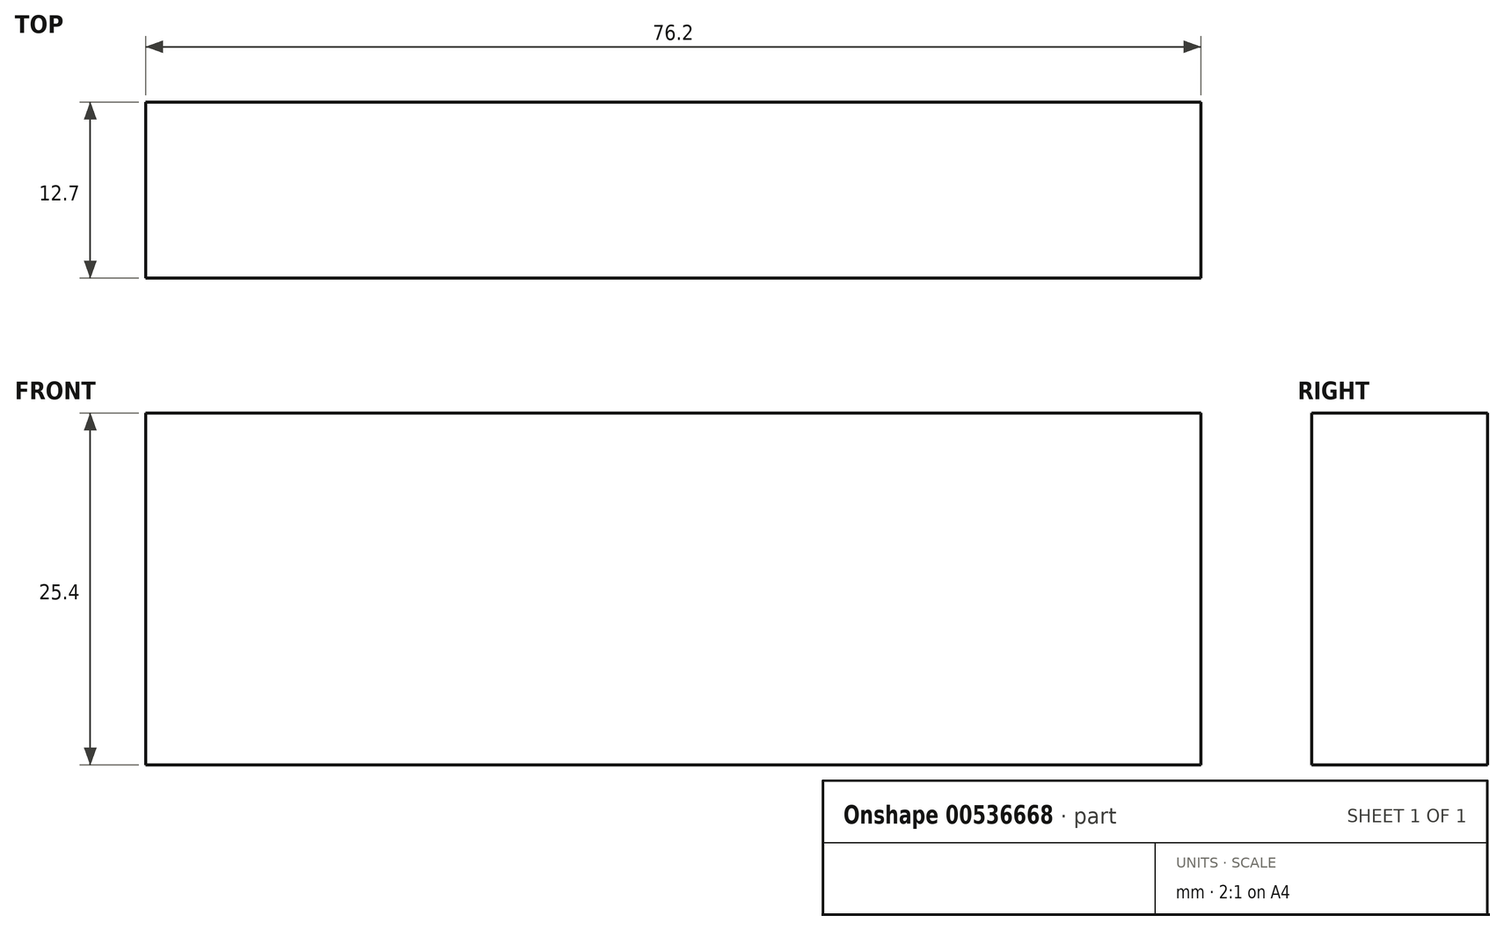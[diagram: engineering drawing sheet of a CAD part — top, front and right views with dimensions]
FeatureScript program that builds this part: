
annotation { "Feature Type Name" : "Feature", "Feature Type Description" : "" }
export const myFeature = defineFeature(function(context is Context, id is Id, definition is map)
    precondition{}
    {
        {
            var Q0;
            Q0=qCreatedBy(makeId("Front.planeOp"),FACE);
            var sketch = newSketch(context, id + "F0", { "sketchPlane" : qUnion([Q0])});
            skLineSegment(sketch, "E0", {"start": v(0, 37.65) * mm, "end": v(0, 12.25) * mm});
            skLineSegment(sketch, "E1", {"start": v(0, 37.65) * mm, "end": v(76.2, 37.65) * mm});
            skLineSegment(sketch, "E2", {"start": v(76.2, 37.65) * mm, "end": v(76.2, 12.25) * mm});
            skLineSegment(sketch, "E3", {"start": v(76.2, 12.25) * mm, "end": v(0, 12.25) * mm});
            skSolve(sketch);
        }
        {
            var Q0;
            Q0=makeQuery(id+"F0.imprint","IMPRINT",FACE,{"disambiguationData":[TD([[makeQuery(id+"F0.imprint","IMPRINT",EDGE,{"derivedFrom":sQuery(id+"F0.wireOp",EDGE,"E0")}),1.0]])]});
            extrude(context, id + "F1", {"entities" : qUnion([Q0]), "depth" : 12.7 * mm, "offsetDistance" : 25.4 * mm});
        }
    });
